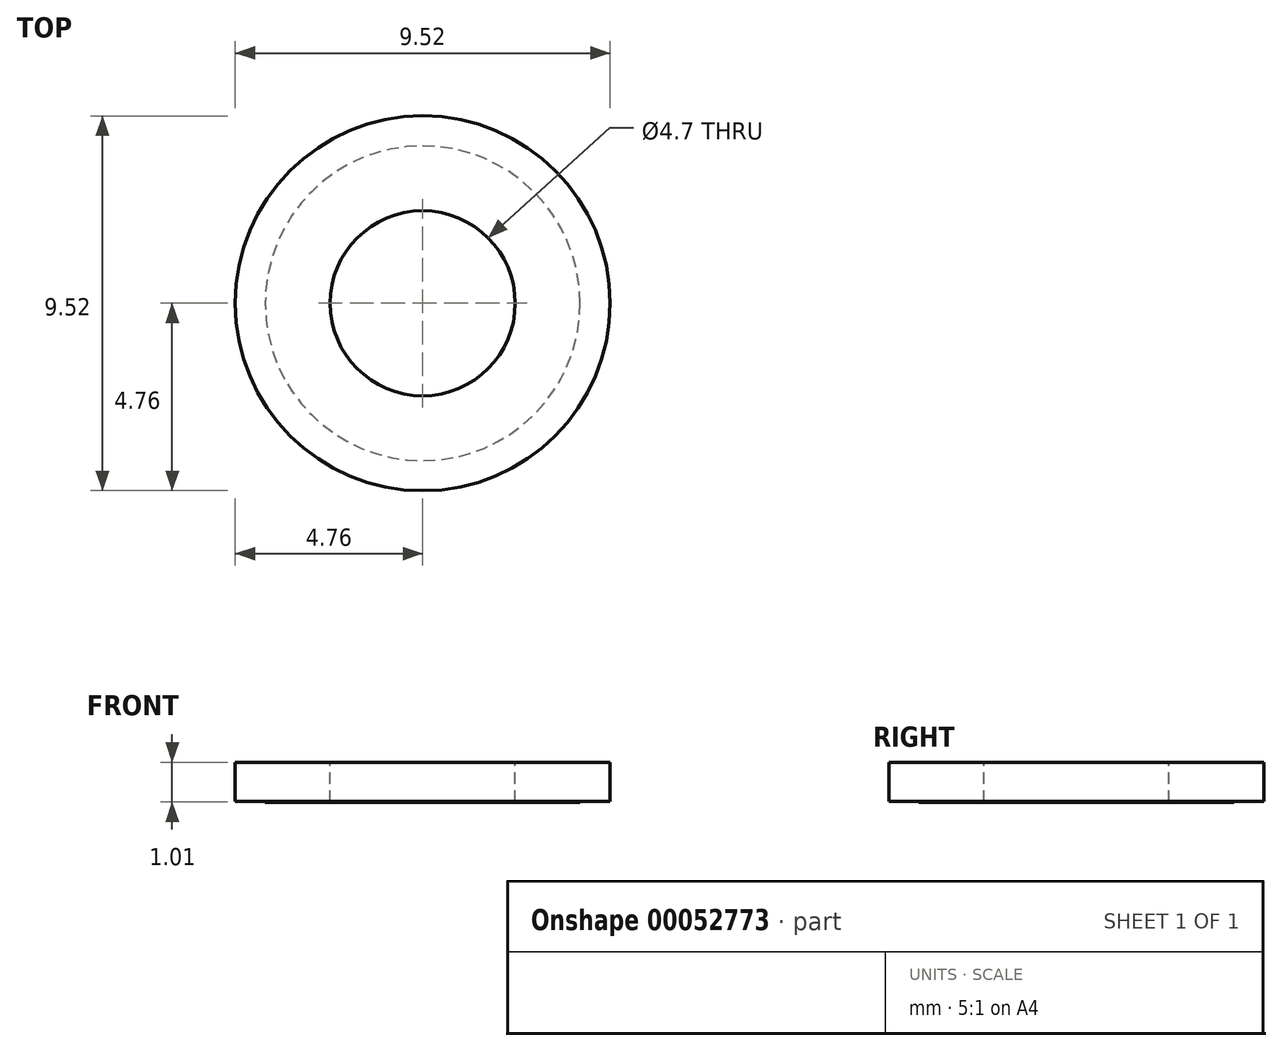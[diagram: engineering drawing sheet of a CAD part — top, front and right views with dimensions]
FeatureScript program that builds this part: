
annotation { "Feature Type Name" : "Feature", "Feature Type Description" : "" }
export const myFeature = defineFeature(function(context is Context, id is Id, definition is map)
    precondition{}
    {
        {
            var Q0;
            Q0=qCreatedBy(makeId("Top.planeOp"),FACE);
            var sketch = newSketch(context, id + "F0", { "sketchPlane" : qUnion([Q0])});
            skCircle(sketch, "E0", {"center": v(0, 0) * mm, "radius": 4.76 * mm});
            skCircle(sketch, "E1", {"center": v(0, 0) * mm, "radius": 4 * mm});
            skCircle(sketch, "E2", {"center": v(0, 0) * mm, "radius": 2.35 * mm});
            skSolve(sketch);
        }
        {
            var Q0;
            Q0=makeQuery(id+"F0.imprint","IMPRINT",FACE,{"disambiguationData":[TD([[makeQuery(id+"F0.imprint","IMPRINT",EDGE,{"derivedFrom":sQuery(id+"F0.wireOp",EDGE,"E1")}),1.0]])]});
            extrude(context, id + "F1", {"entities" : qUnion([Q0]), "oppositeDirection" : true, "depth" : 3 / 203.2 * mm});
        }
        {
            var Q0;
            Q0=makeQuery(id+"F0.imprint","IMPRINT",FACE,{"disambiguationData":[TD([[makeQuery(id+"F0.imprint","IMPRINT",EDGE,{"derivedFrom":sQuery(id+"F0.wireOp",EDGE,"E0")}),1.0]])]});
            var Q1;
            Q1=makeQuery(id+"F0.imprint","IMPRINT",FACE,{"disambiguationData":[TD([[makeQuery(id+"F0.imprint","IMPRINT",EDGE,{"derivedFrom":sQuery(id+"F0.wireOp",EDGE,"E1")}),1.0]])]});
            extrude(context, id + "F2", {"entities" : qUnion([Q0, Q1]), "operationType" : NewBodyOperationType.ADD, "depth" : 1 * mm});
        }
    });
